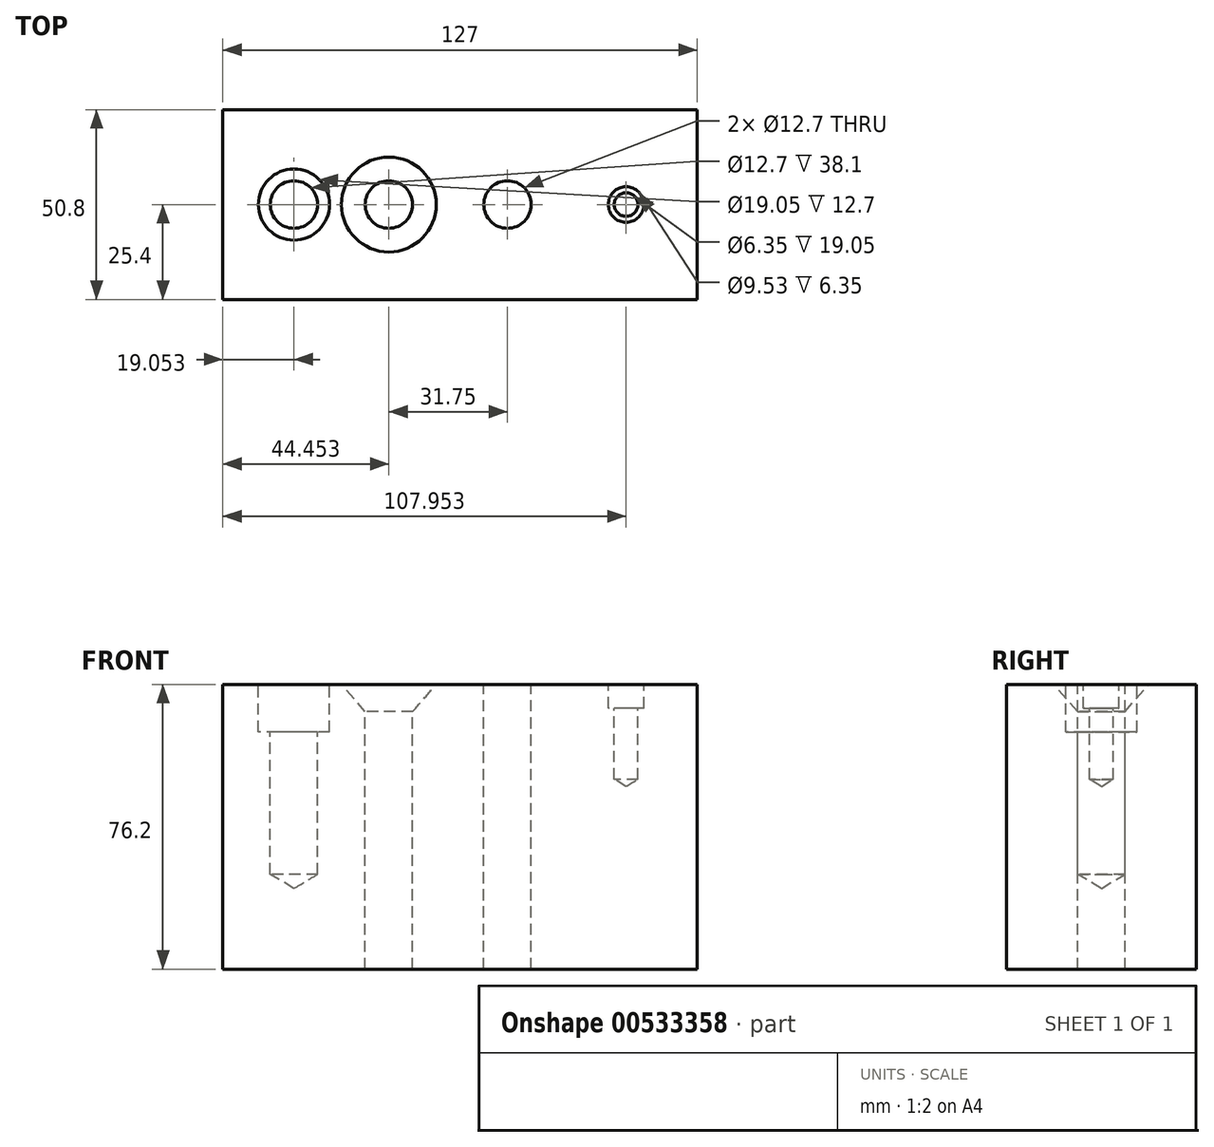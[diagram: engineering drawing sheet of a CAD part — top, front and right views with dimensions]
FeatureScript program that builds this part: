
annotation { "Feature Type Name" : "Feature", "Feature Type Description" : "" }
export const myFeature = defineFeature(function(context is Context, id is Id, definition is map)
    precondition{}
    {
        {
            var Q0;
            Q0=qCreatedBy(makeId("Front.planeOp"),FACE);
            var sketch = newSketch(context, id + "F0", { "sketchPlane" : qUnion([Q0])});
            skLineSegment(sketch, "E0.bottom", {"start": v(-60.64, 76.2) * mm, "end": v(66.36, 76.2) * mm});
            skLineSegment(sketch, "E0.top", {"start": v(-60.64, 0) * mm, "end": v(66.36, 0) * mm});
            skLineSegment(sketch, "E0.left", {"start": v(-60.64, 76.2) * mm, "end": v(-60.64, 0) * mm});
            skLineSegment(sketch, "E0.right", {"start": v(66.36, 76.2) * mm, "end": v(66.36, 0) * mm});
            skSolve(sketch);
        }
        {
            var Q0;
            Q0=makeQuery(id+"F0.imprint","IMPRINT",FACE,{"disambiguationData":[TD([[makeQuery(id+"F0.imprint","IMPRINT",EDGE,{"derivedFrom":sQuery(id+"F0.wireOp",EDGE,"E0.bottom")}),-1.0]])]});
            extrude(context, id + "F1", {"entities" : qUnion([Q0]), "depth" : 50.8 * mm, "offsetDistance" : 25.4 * mm});
        }
        {
            var Q0;
            Q0=makeQuery(id+"F1.opExtrude","SWEPT_FACE",FACE,{"disambiguationData":[OSD([sQuery(id+"F0.wireOp",EDGE,"E0.bottom")])]});
            var sketch = newSketch(context, id + "F2", { "sketchPlane" : qUnion([Q0])});
            skPoint(sketch, "E1", {"position": v(-60.64, -25.4) * mm});
            skPoint(sketch, "E2", {"position": v(66.36, -25.4) * mm});
            skLineSegment(sketch, "E3", {"start": v(-60.64, -25.4) * mm, "end": v(66.36, -25.4) * mm, "construction": true});
            skPoint(sketch, "E4", {"position": v(-41.59, -25.4) * mm});
            skSolve(sketch);
        }
        {
            var Q0;
            Q0=sQuery(id+"F2.wireOp",VERTEX,"E4");
            var Q1;
            Q1=makeQuery(id+"F1.opExtrude","SWEPT_BODY",BODY,{"disambiguationData":[OSD([sQuery(id+"F0.wireOp",EDGE,"E0.bottom"),sQuery(id+"F0.wireOp",EDGE,"E0.top"),sQuery(id+"F0.wireOp",EDGE,"E0.left"),sQuery(id+"F0.wireOp",EDGE,"E0.right")])]});
            hole(context, id + "F3", {"style" : HoleStyle.C_BORE, "endStyle" : HoleEndStyle.BLIND, "holeDiameter" : 12.7 * mm, "cBoreDiameter" : 19.05 * mm, "cBoreDepth" : 12.7 * mm, "holeDepth" : 50.8 * mm, "isTappedThrough" : true, "tappedDepth" : 12.7 * mm, "tapClearance" : 3, "locations" : qUnion([Q0]), "scope" : qUnion([Q1])});
        }
        {
            var Q0;
            Q0=makeQuery(id+"F1.opExtrude","SWEPT_FACE",FACE,{"disambiguationData":[OSD([sQuery(id+"F0.wireOp",EDGE,"E0.bottom")])]});
            var sketch = newSketch(context, id + "F4", { "sketchPlane" : qUnion([Q0])});
            skLineSegment(sketch, "E5", {"start": v(-60.64, -25.4) * mm, "end": v(66.36, -25.4) * mm, "construction": true});
            skPoint(sketch, "E6", {"position": v(-16.19, -25.4) * mm});
            skSolve(sketch);
        }
        {
            var Q0;
            Q0=sQuery(id+"F4.wireOp",VERTEX,"E6");
            var Q1;
            Q1=makeQuery(id+"F1.opExtrude","SWEPT_BODY",BODY,{"disambiguationData":[OSD([sQuery(id+"F0.wireOp",EDGE,"E0.bottom"),sQuery(id+"F0.wireOp",EDGE,"E0.top"),sQuery(id+"F0.wireOp",EDGE,"E0.left"),sQuery(id+"F0.wireOp",EDGE,"E0.right")])]});
            hole(context, id + "F5", {"style" : HoleStyle.C_SINK, "endStyle" : HoleEndStyle.THROUGH, "holeDiameter" : 12.7 * mm, "cSinkDiameter" : 25.4 * mm, "cSinkAngle" : 82 * degree, "isTappedThrough" : true, "tappedDepth" : 12.7 * mm, "tapClearance" : 3, "locations" : qUnion([Q0]), "scope" : qUnion([Q1])});
        }
        {
            var Q0;
            Q0=makeQuery(id+"F1.opExtrude","SWEPT_FACE",FACE,{"disambiguationData":[OSD([sQuery(id+"F0.wireOp",EDGE,"E0.bottom")])]});
            var sketch = newSketch(context, id + "F6", { "sketchPlane" : qUnion([Q0])});
            skPoint(sketch, "E7", {"position": v(-16.19, -25.4) * mm});
            skLineSegment(sketch, "E8", {"start": v(-60.64, -25.4) * mm, "end": v(66.36, -25.4) * mm, "construction": true});
            skPoint(sketch, "E9", {"position": v(15.56, -25.4) * mm});
            skSolve(sketch);
        }
        {
            var Q0;
            Q0=sQuery(id+"F6.wireOp",VERTEX,"E9");
            var Q1;
            Q1=makeQuery(id+"F1.opExtrude","SWEPT_BODY",BODY,{"disambiguationData":[OSD([sQuery(id+"F0.wireOp",EDGE,"E0.bottom"),sQuery(id+"F0.wireOp",EDGE,"E0.top"),sQuery(id+"F0.wireOp",EDGE,"E0.left"),sQuery(id+"F0.wireOp",EDGE,"E0.right")])]});
            hole(context, id + "F7", {"style" : HoleStyle.SIMPLE, "endStyle" : HoleEndStyle.THROUGH, "holeDiameter" : 12.7 * mm, "isTappedThrough" : true, "tappedDepth" : 12.7 * mm, "tapClearance" : 3, "locations" : qUnion([Q0]), "scope" : qUnion([Q1])});
        }
        {
            var Q0;
            Q0=makeQuery(id+"F1.opExtrude","SWEPT_FACE",FACE,{"disambiguationData":[OSD([sQuery(id+"F0.wireOp",EDGE,"E0.bottom")])]});
            var sketch = newSketch(context, id + "F8", { "sketchPlane" : qUnion([Q0])});
            skPoint(sketch, "E10", {"position": v(15.56, -25.4) * mm});
            skLineSegment(sketch, "E11", {"start": v(-60.64, -25.4) * mm, "end": v(66.36, -25.4) * mm, "construction": true});
            skPoint(sketch, "E12", {"position": v(47.31, -25.4) * mm});
            skSolve(sketch);
        }
        {
            var Q0;
            Q0=sQuery(id+"F8.wireOp",VERTEX,"E12");
            var Q1;
            Q1=makeQuery(id+"F1.opExtrude","SWEPT_BODY",BODY,{"disambiguationData":[OSD([sQuery(id+"F0.wireOp",EDGE,"E0.bottom"),sQuery(id+"F0.wireOp",EDGE,"E0.top"),sQuery(id+"F0.wireOp",EDGE,"E0.left"),sQuery(id+"F0.wireOp",EDGE,"E0.right")])]});
            hole(context, id + "F9", {"style" : HoleStyle.C_BORE, "endStyle" : HoleEndStyle.BLIND, "holeDiameter" : 6.35 * mm, "cBoreDiameter" : 9.52 * mm, "cBoreDepth" : 6.35 * mm, "holeDepth" : 25.4 * mm, "isTappedThrough" : true, "tappedDepth" : 12.7 * mm, "tapClearance" : 3, "locations" : qUnion([Q0]), "scope" : qUnion([Q1])});
        }
    });
